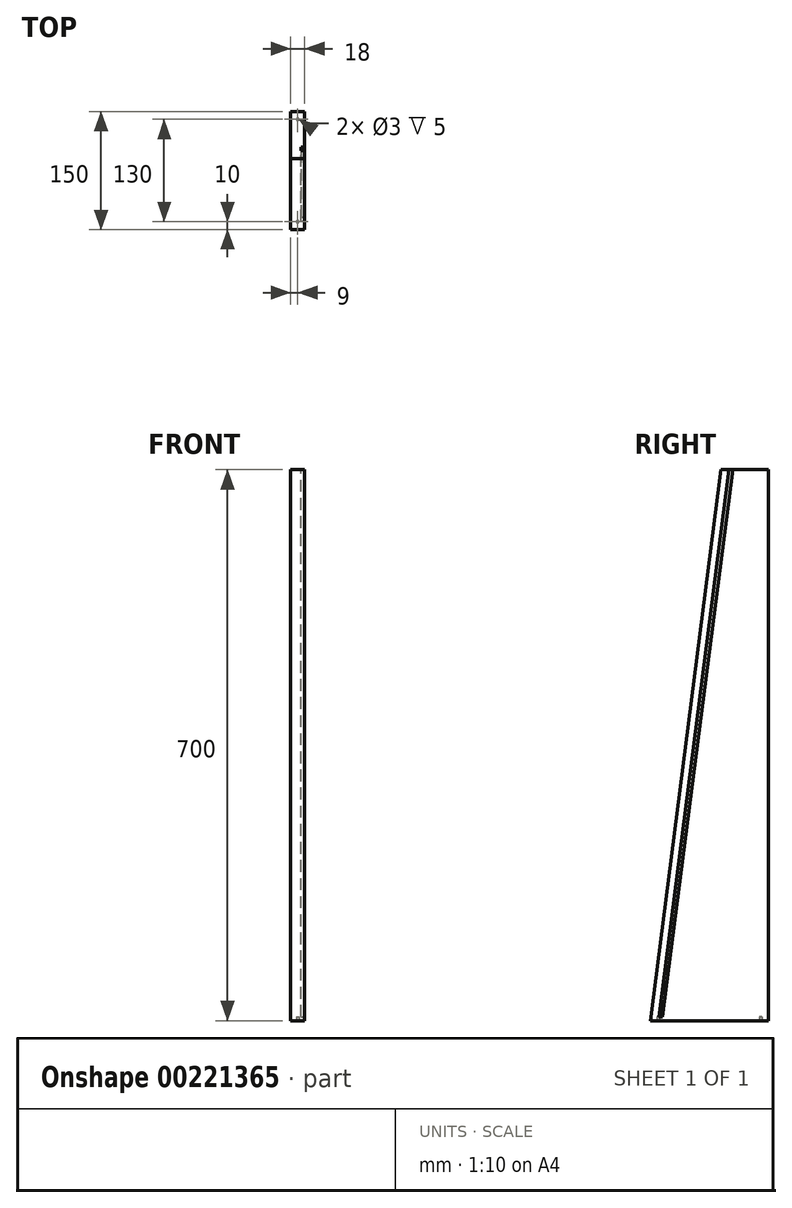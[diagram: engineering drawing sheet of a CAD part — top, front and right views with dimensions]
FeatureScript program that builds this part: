
annotation { "Feature Type Name" : "Feature", "Feature Type Description" : "" }
export const myFeature = defineFeature(function(context is Context, id is Id, definition is map)
    precondition{}
    {
        {
            var Q0;
            Q0=qCreatedBy(makeId("Right.planeOp"),FACE);
            var sketch = newSketch(context, id + "F0", { "sketchPlane" : qUnion([Q0])});
            skLineSegment(sketch, "E0", {"start": v(0, 0) * mm, "end": v(150, 0) * mm});
            skLineSegment(sketch, "E1", {"start": v(150, 0) * mm, "end": v(150, 700) * mm});
            skLineSegment(sketch, "E2", {"start": v(150, 700) * mm, "end": v(90, 700) * mm});
            skLineSegment(sketch, "E3", {"start": v(90, 700) * mm, "end": v(0, 0) * mm});
            skSolve(sketch);
        }
        {
            var Q0;
            Q0 = qSketchRegion(id + "F0", true);
            extrude(context, id + "F1", {"entities" : qUnion([Q0]), "depth" : 18 * mm});
        }
        {
            var Q0;
            Q0=makeQuery(id+"F1.opExtrude","CAP_FACE",FACE,{"disambiguationData":[OSD([sQuery(id+"F0.wireOp",EDGE,"E0"),sQuery(id+"F0.wireOp",EDGE,"E1"),sQuery(id+"F0.wireOp",EDGE,"E2"),sQuery(id+"F0.wireOp",EDGE,"E3")])],"isStart":false});
            var sketch = newSketch(context, id + "F2", { "sketchPlane" : qUnion([Q0])});
            skLineSegment(sketch, "E4", {"start": v(10.64, 5) * mm, "end": v(100, 700) * mm});
            skLineSegment(sketch, "E5", {"start": v(100, 700) * mm, "end": v(105, 700) * mm});
            skLineSegment(sketch, "E6", {"start": v(105, 700) * mm, "end": v(15.64, 5) * mm});
            skLineSegment(sketch, "E7", {"start": v(10.64, 5) * mm, "end": v(15.64, 5) * mm});
            skPoint(sketch, "E8.end.orphan", {"position": v(10, 0) * mm});
            skPoint(sketch, "E9.orphan", {"position": v(15, 0) * mm});
            skSolve(sketch);
        }
        {
            var Q0;
            Q0 = qSketchRegion(id + "F2", true);
            extrude(context, id + "F3", {"entities" : qUnion([Q0]), "operationType" : NewBodyOperationType.REMOVE, "oppositeDirection" : true, "depth" : 5 * mm});
        }
        {
            var Q0;
            Q0=makeQuery(id+"F1.opExtrude","SWEPT_FACE",FACE,{"disambiguationData":[OSD([sQuery(id+"F0.wireOp",EDGE,"E0")])]});
            var sketch = newSketch(context, id + "F4", { "sketchPlane" : qUnion([Q0])});
            skCircle(sketch, "E10", {"center": v(9, -10) * mm, "radius": 1.5 * mm});
            skCircle(sketch, "E11", {"center": v(9, -140) * mm, "radius": 1.5 * mm});
            skSolve(sketch);
        }
        {
            var Q0;
            Q0 = qSketchRegion(id + "F4", true);
            extrude(context, id + "F5", {"entities" : qUnion([Q0]), "operationType" : NewBodyOperationType.REMOVE, "oppositeDirection" : true, "depth" : 5 * mm});
        }
    });
